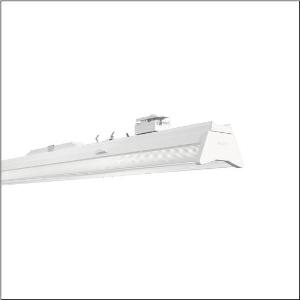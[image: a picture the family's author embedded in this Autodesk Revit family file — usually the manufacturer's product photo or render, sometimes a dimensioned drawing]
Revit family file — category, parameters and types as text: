
# Revit family: licross_11_performance_ho_51tm16dn4fxm
name_source: partatom
category: Lighting Fixtures
units: mm (PartAtom-declared; Revit-internal decimal feet)

## family parameters
Cut with Voids When Loaded = No
Host = Face
Light Source = No
Part Type = Normal
Room Calculation Point = No
Round Connector Dimension = Use Diameter
Shared = No

## types (1)
- --- (1 x LED, 15460 lm, 87.3 W, 4000K)
    Apparent Load = 87 VA
    CIE Flux Codes = 63 87 95 78 100
    Color Rendering = 80
    Color Temperature = 4000K
    Default Elevation = 1800 mm
    Description = Licross 11 Performance HO, luminaire insert, of sheet steel, galvanised, coil coated, white, length: 1.500mm, width: 120mm, height: 123mm, LED rated luminous flux: 15.460lm, light colour: 840, SDCM (Standard Deviation of Colour Matching)MacAdam ≤ 2 SDCM (initial), control gear: DALI 2, with plug, 5-pole, with phase selection, mains connection: 220..240V, AC, 50/60Hz, rated input power: 87W, internal wiring halogen-free, primary light control with lens, of plastic, primary optical cover: cover, of PMMA, light emission: direct/indirect distribution, primary light characteristic: symmetric, protection rating (complete): IP40, insulation class (complete): insulation class I (protective earthing), certification: CE, ENEC, VDE, UKCA, protection symbol: D if used in an environment without relevant dust loads with corresponding accessories, impact resistance: IK06, permissible ambient temperature for indoor applications: -25..+30°C, corresponds to IFS (International Featured Standards) requirements for safety and quality in the food industry, reducing of maximum allowable ambient temperature of 5°C with ceiling mounting, LABS conformity tested according to VDMA 24364:2018-05, The light source and the operating device comply with the requirements of the Ecodesign Regulation (EU) 2019/2020 and are replaceable in accordance with this regulation, packaging unit: 1 piece
    Height = 114 mm
    Lamp = 1 x LED
    Lamp Light Flux = 15460 lm
    Lamp Power = 87.3 W
    Lamp count = 1
    Length = 1500 mm
    Luminous efficacy = 177 lm/W
    Manufacturer = Siteco
    ModVariant = No
    Model = 51TM16DN4FXM
    Mounting Place = Ceiling
    Mounting Type = Pendant
    Number of Poles = 1
    OnlyDefault = Yes
    Power Factor = 1
    Product Name = Licross 11 Performance HO
    Product group = luminaire insert | ceiling pendant
    ProductGroupID = 901
    Protection Class = Protection class I
    Protection Degree = IP 40
    RLX_Detail_Level = 1
    RLX_Emergency_Light_Flux = 0 lm
    RLX_Emergency_Type = 0
    RLX_Emergency_Type_DB = No
    RlxData = <blob elided: 34297 chars, md5=a51a1237>
    Socket = socket
    Standby Power = 0 W
    System Light Flux = 15460 lm
    System Power = 87 W
    Type Comments = factory setting: luminous flux: 100 % | dim-lin: 254 | 589 mA
    Type Image = l_1256138.jpg
    URL = http://relux.com
    VarID = @adj_104533
    Voltage = 0 V
    Weight = 0.00 kg
    Width = 120 mm

## geometry (parser evidence)
native form markers: Blend x4, Sweep x12
no freeform markers — native parametric forms only
